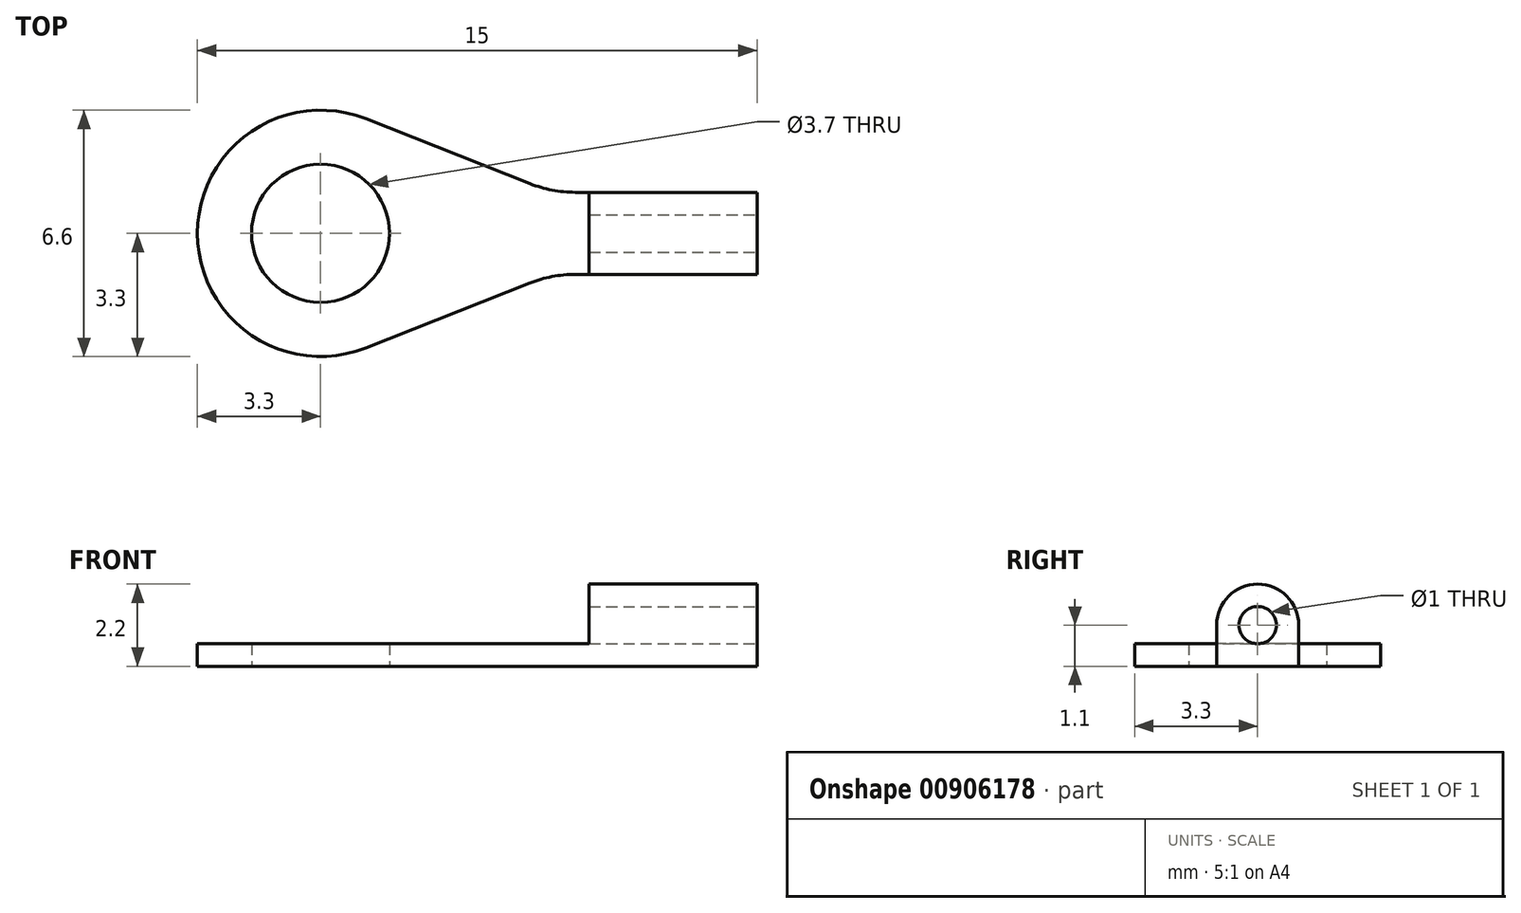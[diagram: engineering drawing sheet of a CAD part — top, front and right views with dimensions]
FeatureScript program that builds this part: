
annotation { "Feature Type Name" : "Feature", "Feature Type Description" : "" }
export const myFeature = defineFeature(function(context is Context, id is Id, definition is map)
    precondition{}
    {
        {
            var Q0;
            Q0=qCreatedBy(makeId("Top.planeOp"),FACE);
            var sketch = newSketch(context, id + "F0", { "sketchPlane" : qUnion([Q0])});
            skLineSegment(sketch, "E0", {"start": v(15, 2.2) * mm, "end": v(15, 4.4) * mm});
            skLineSegment(sketch, "E1", {"start": v(0, 3.3) * mm, "end": v(0, 3.3) * mm});
            skPoint(sketch, "E2.visualSharp", {"position": v(0, 6.6) * mm});
            skArc(sketch, "E2.filletArc", {"start": v(3.3, 6.6) * mm, "mid": v(0.97, 5.63) * mm, "end": v(0, 3.3) * mm});
            skPoint(sketch, "E3.visualSharp", {"position": v(0, 0) * mm});
            skArc(sketch, "E3.filletArc", {"start": v(0, 3.3) * mm, "mid": v(0.97, 0.97) * mm, "end": v(3.3, 0) * mm});
            skLineSegment(sketch, "E4.0", {"start": v(10.5, 2.2) * mm, "end": v(10.5, 4.4) * mm});
            skLineSegment(sketch, "E5.0", {"start": v(9.5, 2.14) * mm, "end": v(9.5, 4.46) * mm});
            skLineSegment(sketch, "E6.0", {"start": v(3.3, 0) * mm, "end": v(3.3, 6.6) * mm});
            skCircle(sketch, "E7", {"center": v(3.3, 3.3) * mm, "radius": 1.85 * mm});
            skLineSegment(sketch, "E8", {"start": v(15, 3.3) * mm, "end": v(9.5, 3.3) * mm});
            skPoint(sketch, "E9.orphan", {"position": v(10.5, 3.3) * mm});
            skLineSegment(sketch, "E10.0", {"start": v(15, 4.4) * mm, "end": v(10.13, 4.4) * mm});
            skLineSegment(sketch, "E11.0", {"start": v(15, 2.2) * mm, "end": v(10.13, 2.2) * mm});
            skArc(sketch, "E12", {"start": v(4.51, 6.37) * mm, "mid": v(0, 3.3) * mm, "end": v(4.51, 0.23) * mm});
            skLineSegment(sketch, "E13", {"start": v(8.92, 4.63) * mm, "end": v(4.51, 6.37) * mm});
            skLineSegment(sketch, "E14", {"start": v(8.92, 1.97) * mm, "end": v(4.51, 0.23) * mm});
            skPoint(sketch, "E15.visualSharp", {"position": v(9.5, 4.4) * mm});
            skArc(sketch, "E15.filletArc", {"start": v(8.92, 4.63) * mm, "mid": v(9.51, 4.46) * mm, "end": v(10.13, 4.4) * mm});
            skPoint(sketch, "E16.visualSharp", {"position": v(9.5, 2.2) * mm});
            skArc(sketch, "E16.filletArc", {"start": v(10.13, 2.2) * mm, "mid": v(9.51, 2.14) * mm, "end": v(8.92, 1.97) * mm});
            skPoint(sketch, "E17.orphan", {"position": v(15, 6.6) * mm});
            skPoint(sketch, "E18.orphan", {"position": v(10.5, 6.6) * mm});
            skPoint(sketch, "E19.orphan", {"position": v(15, 0) * mm});
            skPoint(sketch, "E20.orphan", {"position": v(10.5, 0) * mm});
            skSolve(sketch);
        }
        {
            var Q0;
            Q0 = qSketchRegion(id + "F0", true);
            extrude(context, id + "F1", {"entities" : qUnion([Q0]), "depth" : 0.6 * mm, "offsetDistance" : 25 * mm});
        }
        {
            var Q0;
            Q0=makeQuery(id+"F1.opExtrude","CAP_FACE",FACE,{"disambiguationData":[OSD([sQuery(id+"F0.wireOp",EDGE,"E0"),sQuery(id+"F0.wireOp",EDGE,"E7"),sQuery(id+"F0.wireOp",EDGE,"E10.0"),sQuery(id+"F0.wireOp",EDGE,"E11.0"),sQuery(id+"F0.wireOp",EDGE,"E12"),sQuery(id+"F0.wireOp",EDGE,"E13"),sQuery(id+"F0.wireOp",EDGE,"E14"),sQuery(id+"F0.wireOp",EDGE,"E15.filletArc"),sQuery(id+"F0.wireOp",EDGE,"E16.filletArc")])],"isStart":false});
            var sketch = newSketch(context, id + "F2", { "sketchPlane" : qUnion([Q0])});
            skLineSegment(sketch, "E21.bottom", {"start": v(15, 4.4) * mm, "end": v(10.5, 4.4) * mm});
            skLineSegment(sketch, "E21.top", {"start": v(15, 2.2) * mm, "end": v(10.5, 2.2) * mm});
            skLineSegment(sketch, "E21.left", {"start": v(15, 4.4) * mm, "end": v(15, 2.2) * mm});
            skLineSegment(sketch, "E21.right", {"start": v(10.5, 4.4) * mm, "end": v(10.5, 2.2) * mm});
            skSolve(sketch);
        }
        {
            var Q0;
            Q0=makeQuery(id+"F2.imprint","IMPRINT",FACE,{"disambiguationData":[TD([[makeQuery(id+"F2.imprint","IMPRINT",EDGE,{"derivedFrom":sQuery(id+"F2.wireOp",EDGE,"E21.bottom")}),1.0]])]});
            extrude(context, id + "F3", {"entities" : qUnion([Q0]), "operationType" : NewBodyOperationType.ADD, "depth" : 1.6 * mm, "offsetDistance" : 25 * mm});
        }
        {
            var Q0;
            Q0=makeQuery(id+"F3.opExtrude","CAP_EDGE",EDGE,{"disambiguationData":[OSD([sQuery(id+"F2.wireOp",EDGE,"E21.top")])],"isStart":false});
            var Q1;
            Q1=makeQuery(id+"F3.opExtrude","CAP_EDGE",EDGE,{"disambiguationData":[OSD([sQuery(id+"F2.wireOp",EDGE,"E21.bottom")])],"isStart":false});
            fillet(context, id + "F4", {"entities" : qUnion([Q0, Q1]), "radius" : 1.1 * mm, "tangentPropagation" : true, "allowEdgeOverflow" : false});
        }
        {
            var Q0;
            Q0=makeQuery(id+"F3.boolean.opBoolean","MERGE",FACE,{"derivedFrom":[makeQuery(id+"F1.opExtrude","SWEPT_FACE",FACE,{"disambiguationData":[OSD([sQuery(id+"F0.wireOp",EDGE,"E0")])]}),makeQuery(id+"F3.opExtrude","SWEPT_FACE",FACE,{"disambiguationData":[OSD([sQuery(id+"F2.wireOp",EDGE,"E21.left")])]})]});
            var sketch = newSketch(context, id + "F5", { "sketchPlane" : qUnion([Q0])});
            skCircle(sketch, "E22", {"center": v(3.3, 1.1) * mm, "radius": 0.5 * mm});
            skSolve(sketch);
        }
        {
            var Q0;
            Q0=makeQuery(id+"F5.imprint","IMPRINT",FACE,{"disambiguationData":[TD([[makeQuery(id+"F5.imprint","IMPRINT",EDGE,{"derivedFrom":sQuery(id+"F5.wireOp",EDGE,"E22")}),1.0]])]});
            extrude(context, id + "F6", {"entities" : qUnion([Q0]), "operationType" : NewBodyOperationType.REMOVE, "oppositeDirection" : true, "depth" : 25 * mm, "offsetDistance" : 25 * mm});
        }
    });
